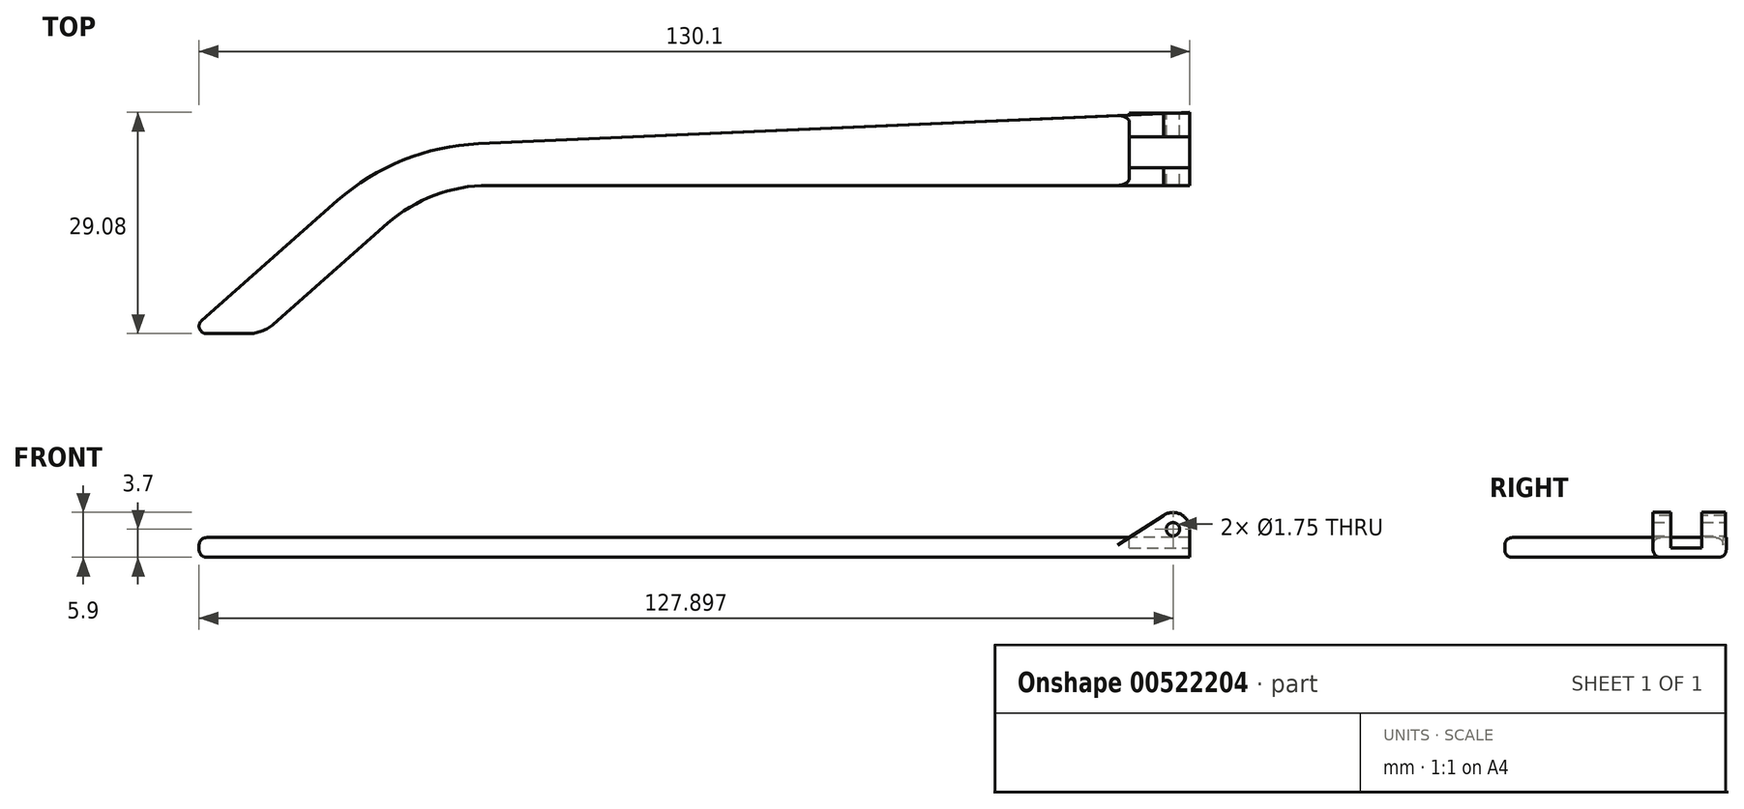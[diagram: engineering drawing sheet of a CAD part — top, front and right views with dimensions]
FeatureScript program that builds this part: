
annotation { "Feature Type Name" : "Feature", "Feature Type Description" : "" }
export const myFeature = defineFeature(function(context is Context, id is Id, definition is map)
    precondition{}
    {
        {
            var Q0;
            Q0=qCreatedBy(makeId("Top.planeOp"),FACE);
            var sketch = newSketch(context, id + "F0", { "sketchPlane" : qUnion([Q0])});
            skLineSegment(sketch, "E0", {"start": v(61.85, 18.06) * mm, "end": v(-42.15, 13.46) * mm});
            skLineSegment(sketch, "E1", {"start": v(-42.15, 13.46) * mm, "end": v(-69.9, -11.02) * mm});
            skLineSegment(sketch, "E2", {"start": v(-69.9, -11.02) * mm, "end": v(-59.9, -11.02) * mm});
            skLineSegment(sketch, "E3", {"start": v(-59.9, -11.02) * mm, "end": v(-37.82, 8.46) * mm});
            skLineSegment(sketch, "E4", {"start": v(-37.82, 8.46) * mm, "end": v(61.85, 8.46) * mm});
            skLineSegment(sketch, "E5", {"start": v(61.85, 8.46) * mm, "end": v(61.85, 18.06) * mm});
            skSolve(sketch);
        }
        {
            var Q0;
            Q0=makeQuery(id+"F0.imprint","IMPRINT",FACE,{"disambiguationData":[TD([[makeQuery(id+"F0.imprint","IMPRINT",EDGE,{"derivedFrom":sQuery(id+"F0.wireOp",EDGE,"E0")}),1.0]])]});
            extrude(context, id + "F1", {"entities" : qUnion([Q0]), "depth" : 2.6 * mm, "offsetDistance" : 25 * mm});
        }
        {
            var Q0;
            Q0=makeQuery(id+"F1.opExtrude","SWEPT_EDGE",EDGE,{"disambiguationData":[OSD([sQuery(id+"F0.wireOp",EDGE,"E0"),sQuery(id+"F0.wireOp",EDGE,"E1")])]});
            fillet(context, id + "F2", {"entities" : qUnion([Q0]), "radius" : 30 * mm, "tangentPropagation" : true, "allowEdgeOverflow" : false});
        }
        {
            var Q0;
            Q0=makeQuery(id+"F1.opExtrude","SWEPT_EDGE",EDGE,{"disambiguationData":[OSD([sQuery(id+"F0.wireOp",EDGE,"E1"),sQuery(id+"F0.wireOp",EDGE,"E2")])]});
            fillet(context, id + "F3", {"entities" : qUnion([Q0]), "radius" : 1 * mm, "tangentPropagation" : true, "allowEdgeOverflow" : false});
        }
        {
            var Q0;
            Q0=makeQuery(id+"F1.opExtrude","SWEPT_EDGE",EDGE,{"disambiguationData":[OSD([sQuery(id+"F0.wireOp",EDGE,"E2"),sQuery(id+"F0.wireOp",EDGE,"E3")])]});
            fillet(context, id + "F4", {"entities" : qUnion([Q0]), "radius" : 5 * mm, "tangentPropagation" : true, "allowEdgeOverflow" : false});
        }
        {
            var Q0;
            Q0=makeQuery(id+"F1.opExtrude","SWEPT_EDGE",EDGE,{"disambiguationData":[OSD([sQuery(id+"F0.wireOp",EDGE,"E3"),sQuery(id+"F0.wireOp",EDGE,"E4")])]});
            fillet(context, id + "F5", {"entities" : qUnion([Q0]), "radius" : 20 * mm, "tangentPropagation" : true, "allowEdgeOverflow" : false});
        }
        {
            var Q0;
            Q0=makeQuery(id+"F1.opExtrude","SWEPT_FACE",FACE,{"disambiguationData":[OSD([sQuery(id+"F0.wireOp",EDGE,"E4")])]});
            var sketch = newSketch(context, id + "F6", { "sketchPlane" : qUnion([Q0])});
            skCircle(sketch, "E6", {"center": v(59.65, 3.7) * mm, "radius": 2.2 * mm});
            skLineSegment(sketch, "E7", {"start": v(58.4, 5.51) * mm, "end": v(53.93, 2.6) * mm});
            skLineSegment(sketch, "E8", {"start": v(53.93, 2.6) * mm, "end": v(57.74, 2.6) * mm});
            skLineSegment(sketch, "E9", {"start": v(61.85, 2.6) * mm, "end": v(61.85, 3.7) * mm});
            skSolve(sketch);
        }
        {
            var Q0;
            {var subQ0=sQuery(id+"F6.wireOp",EDGE,"E6");var subQ1=makeQuery(id+"F1.opExtrude","CAP_EDGE",EDGE,{"disambiguationData":[OSD([sQuery(id+"F0.wireOp",EDGE,"E4")])],"isStart":false});var subQ2=makeQuery(id+"F6.imprint","INTERSECT",VERTEX,{"disambiguationData":[OD(0.0)],"derivedFrom":[subQ1,subQ0]});Q0=makeQuery(id+"F6.imprint","IMPRINT",FACE,{"disambiguationData":[TD([[makeQuery(id+"F6.imprint","IMPRINT",EDGE,{"disambiguationData":[TD([[subQ2,-1.0]])],"derivedFrom":subQ0}),1.0]])]});}
            var Q1;
            {var subQ0=sQuery(id+"F6.wireOp",EDGE,"E7");Q1=makeQuery(id+"F6.imprint","IMPRINT",FACE,{"disambiguationData":[TD([[makeQuery(id+"F6.imprint","IMPRINT",EDGE,{"derivedFrom":subQ0}),1.0]])]});}
            var Q2;
            {var subQ0=sQuery(id+"F6.wireOp",EDGE,"E9");Q2=makeQuery(id+"F6.imprint","IMPRINT",FACE,{"disambiguationData":[TD([[makeQuery(id+"F6.imprint","IMPRINT",EDGE,{"derivedFrom":subQ0}),1.0]])]});}
            extrude(context, id + "F7", {"entities" : qUnion([Q0, Q1, Q2]), "operationType" : NewBodyOperationType.ADD, "oppositeDirection" : true, "depth" : 9.5 * mm, "offsetDistance" : 25 * mm});
        }
        {
            var Q0;
            {var subQ1=sQuery(id+"F0.wireOp",EDGE,"E4");var subQ2=sQuery(id+"F0.wireOp",EDGE,"E3");Q0=makeQuery(id+"F7.boolean.opBoolean","SPLIT",EDGE,{"disambiguationData":[TD([makeQuery(id+"F5.opFillet","BLEND_FACE",FACE,{"disambiguationData":[OSD([subQ2,subQ1])]})])],"derivedFrom":makeQuery(id+"F1.opExtrude","CAP_EDGE",EDGE,{"disambiguationData":[OSD([subQ1])],"isStart":false})});}
            var Q1;
            Q1=makeQuery(id+"F1.opExtrude","CAP_EDGE",EDGE,{"disambiguationData":[OSD([sQuery(id+"F0.wireOp",EDGE,"E0")])],"isStart":true});
            fillet(context, id + "F8", {"entities" : qUnion([Q0, Q1]), "radius" : 1 * mm, "tangentPropagation" : true, "allowEdgeOverflow" : false});
        }
        {
            var Q0;
            {var subQ0=sQuery(id+"F0.wireOp",EDGE,"E3");var subQ1=sQuery(id+"F0.wireOp",EDGE,"E2");var subQ4=sQuery(id+"F0.wireOp",EDGE,"E4");var subQ5=sQuery(id+"F0.wireOp",EDGE,"E1");var subQ6=sQuery(id+"F0.wireOp",EDGE,"E0");Q0=makeQuery(id+"F7.boolean.opBoolean","SPLIT",FACE,{"disambiguationData":[TD([makeQuery(id+"F1.opExtrude","SWEPT_FACE",FACE,{"disambiguationData":[OSD([subQ5])]})])],"derivedFrom":makeQuery(id+"F1.opExtrude","CAP_FACE",FACE,{"disambiguationData":[OSD([subQ6,subQ5,subQ1,subQ0,subQ4,sQuery(id+"F0.wireOp",EDGE,"E5")])],"isStart":false})});}
            var sketch = newSketch(context, id + "F9", { "sketchPlane" : qUnion([Q0])});
            skLineSegment(sketch, "E10.bottom", {"start": v(53.93, 14.86) * mm, "end": v(61.88, 14.86) * mm});
            skLineSegment(sketch, "E10.top", {"start": v(53.93, 10.76) * mm, "end": v(61.88, 10.76) * mm});
            skLineSegment(sketch, "E10.left", {"start": v(53.93, 14.86) * mm, "end": v(53.93, 10.76) * mm});
            skLineSegment(sketch, "E10.right", {"start": v(61.88, 14.86) * mm, "end": v(61.88, 10.76) * mm});
            skSolve(sketch);
        }
        {
            var Q0;
            Q0 = qSketchRegion(id + "F9", true);
            var Q1;
            Q1=makeQuery(id+"F9.imprint","IMPRINT",FACE,{"disambiguationData":[TD([[makeQuery(id+"F9.imprint","IMPRINT",EDGE,{"derivedFrom":sQuery(id+"F9.wireOp",EDGE,"E10.bottom")}),-1.0]])]});
            extrude(context, id + "F10", {"entities" : qUnion([Q0, Q1]), "operationType" : NewBodyOperationType.REMOVE, "depth" : 5 * mm, "offsetDistance" : 25 * mm});
        }
        {
            var Q0;
            Q0=makeQuery(id+"F9.imprint","IMPRINT",FACE,{"disambiguationData":[TD([[makeQuery(id+"F9.imprint","IMPRINT",EDGE,{"derivedFrom":sQuery(id+"F9.wireOp",EDGE,"E10.bottom")}),-1.0]])]});
            extrude(context, id + "F11", {"entities" : qUnion([Q0]), "operationType" : NewBodyOperationType.REMOVE, "oppositeDirection" : true, "depth" : 1.4 * mm, "offsetDistance" : 25 * mm});
        }
        {
            var Q0;
            Q0=sQuery(id+"F6.wireOp",VERTEX,"E6.center");
            var Q1;
            Q1=makeQuery(id+"F1.opExtrude","SWEPT_BODY",BODY,{"disambiguationData":[OSD([sQuery(id+"F0.wireOp",EDGE,"E0"),sQuery(id+"F0.wireOp",EDGE,"E1"),sQuery(id+"F0.wireOp",EDGE,"E2"),sQuery(id+"F0.wireOp",EDGE,"E3"),sQuery(id+"F0.wireOp",EDGE,"E4"),sQuery(id+"F0.wireOp",EDGE,"E5")])]});
            hole(context, id + "F12", {"style" : HoleStyle.SIMPLE, "endStyle" : HoleEndStyle.THROUGH, "holeDiameter" : 1.75 * mm, "majorDiameter" : 5 * mm, "isTappedThrough" : true, "tappedDepth" : 12 * mm, "tapClearance" : 3, "locations" : qUnion([Q0]), "scope" : qUnion([Q1])});
        }
    });
